# Revit family: 29100001_35015001
name_source: partatom
category: Plumbing Fixtures
revit_build: Autodesk Revit 2014 (Build: 20130308_1515(x64)
units: mm (PartAtom-declared; Revit-internal decimal feet)

## types (2) — shared parameters
ADA Compliant = No
Assembly Code = D2010710
CW Connection = Yes
CWFU = 3
Cold Water Connection Diameter = 1/2"
Cold Water Connection Radius = 1/4"
Default Elevation = 44"
HW Connection = Yes
HWFU = 3
Height = 40"
Hot Water Connection Diameter = 1"
Hot Water Connection Radius = 1/4"
Installation Type = Wall Mounted
Length = 2 15/16"
Manufacturer = Grohe
Price = Prices may vary. Please consult Manufacturer Representative for most up-to-date price list.
Tempered Connection Diameter = 1/2"
Tempered Connection Radius = 1/4"
Vent Connection = No
WFU = 4
Warranty Documentation Link = https://cdn.cloud.grohe.com
Waste Connection = No

## per-type parameters (varying)
| type | Description | Finish | Flow Rate | Material | Product Page URL | URL | Width |
| 29100001 | Concetto Pressure Balance Valve Trim | Metal-Grohe-001-Chrome |  | Metal-Grohe-001-Chrome | https://www.grohe.us | https://www.grohe.us | 7 5/16" |
| 35010EN1 | Concetto Pressure Balance Valve Shower Combination | Metal-Grohe-EN1-Brushed Nickel | 5.3 gpm (20 L/min) | Metal-Grohe-EN1-Brushed Nickel | https://www.grohe.ca | https://www.grohe.com | 6 11/16" |

note: column(s) folded — value = type name in every type: Model

## geometry (parser evidence)
native form markers: Sweep x8
no freeform markers — native parametric forms only
